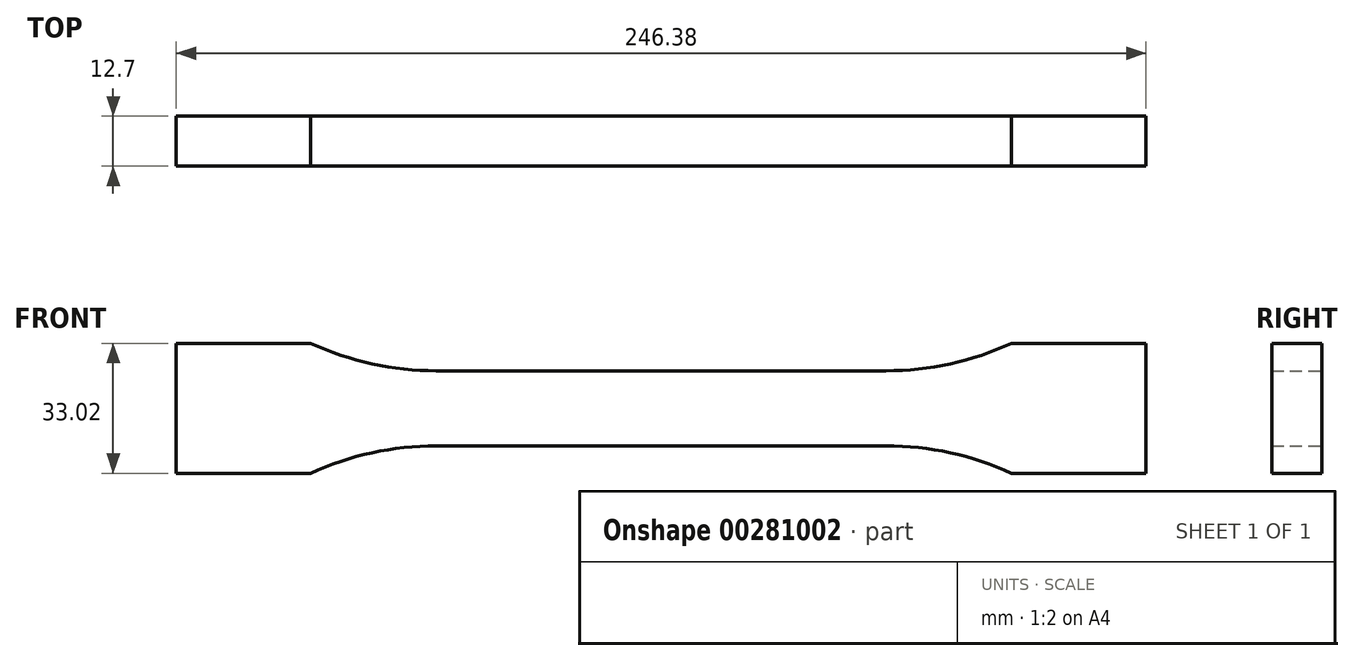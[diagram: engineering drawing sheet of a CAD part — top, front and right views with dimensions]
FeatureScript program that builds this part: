
annotation { "Feature Type Name" : "Feature", "Feature Type Description" : "" }
export const myFeature = defineFeature(function(context is Context, id is Id, definition is map)
    precondition{}
    {
        {
            var Q0;
            Q0=qCreatedBy(makeId("Front.planeOp"),FACE);
            var sketch = newSketch(context, id + "F0", { "sketchPlane" : qUnion([Q0])});
            skLineSegment(sketch, "E0", {"start": v(0, 9.52) * mm, "end": v(57.15, 9.52) * mm});
            skArc(sketch, "E1", {"start": v(57.15, 9.53) * mm, "mid": v(73.46, 11.3) * mm, "end": v(89.02, 16.51) * mm});
            skLineSegment(sketch, "E2", {"start": v(89.02, 16.51) * mm, "end": v(123.2, 16.51) * mm});
            skLineSegment(sketch, "E3", {"start": v(123.2, 16.51) * mm, "end": v(123.2, 0) * mm});
            skLineSegment(sketch, "E4.MirrorCS", {"start": v(0, -9.52) * mm, "end": v(57.15, -9.52) * mm});
            skLineSegment(sketch, "E5.MirrorCS", {"start": v(123.2, -16.51) * mm, "end": v(123.2, 0) * mm});
            skLineSegment(sketch, "E6.MirrorCS", {"start": v(89.02, -16.51) * mm, "end": v(123.2, -16.51) * mm});
            skArc(sketch, "E7.MirrorCS", {"start": v(57.15, -9.53) * mm, "mid": v(73.46, -11.3) * mm, "end": v(89.02, -16.51) * mm});
            skArc(sketch, "E8.MirrorCS", {"start": v(-57.15, -9.53) * mm, "mid": v(-73.46, -11.3) * mm, "end": v(-89.02, -16.51) * mm});
            skLineSegment(sketch, "E9.MirrorCS", {"start": v(-89.02, -16.5) * mm, "end": v(-123.2, -16.5) * mm});
            skArc(sketch, "E10.MirrorCS", {"start": v(-57.15, 9.53) * mm, "mid": v(-73.46, 11.3) * mm, "end": v(-89.02, 16.51) * mm});
            skLineSegment(sketch, "E11.MirrorCS", {"start": v(-89.02, 16.51) * mm, "end": v(-123.2, 16.51) * mm});
            skLineSegment(sketch, "E12.MirrorCS", {"start": v(-123.2, -16.51) * mm, "end": v(-123.2, 0) * mm});
            skLineSegment(sketch, "E13.MirrorCS", {"start": v(0, -9.52) * mm, "end": v(-57.15, -9.53) * mm});
            skLineSegment(sketch, "E14.MirrorCS", {"start": v(-123.2, 16.51) * mm, "end": v(-123.2, 0) * mm});
            skLineSegment(sketch, "E15.MirrorCS", {"start": v(0, 9.52) * mm, "end": v(-57.15, 9.52) * mm});
            skSolve(sketch);
        }
        {
            var Q0;
            Q0 = qSketchRegion(id + "F0", true);
            extrude(context, id + "F1", {"entities" : qUnion([Q0]), "depth" : 12.7 * mm});
        }
    });
